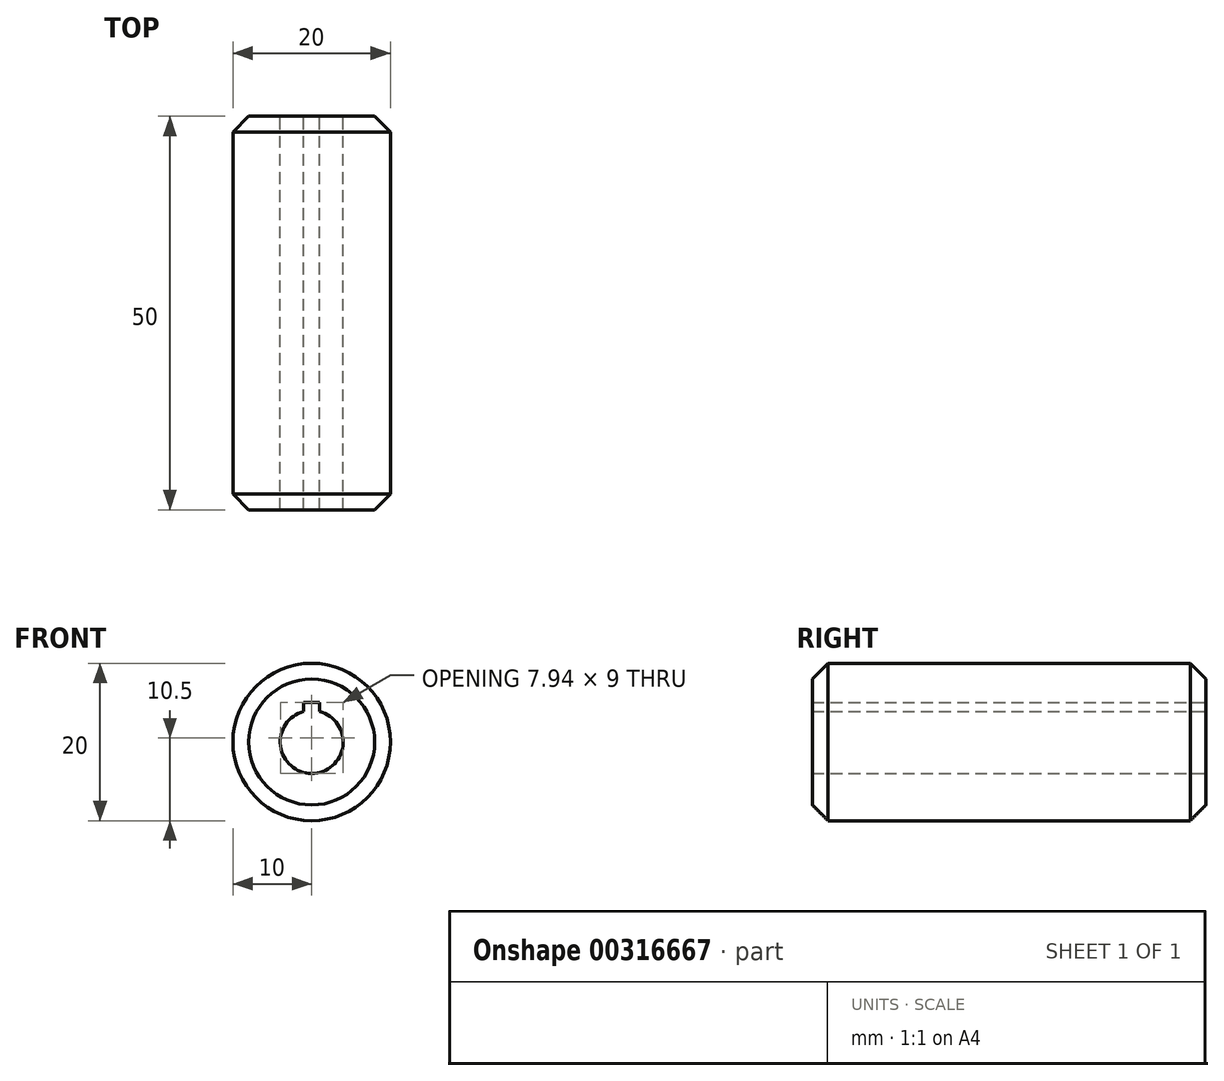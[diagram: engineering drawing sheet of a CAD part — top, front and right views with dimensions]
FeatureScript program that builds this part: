
annotation { "Feature Type Name" : "Feature", "Feature Type Description" : "" }
export const myFeature = defineFeature(function(context is Context, id is Id, definition is map)
    precondition{}
    {
        {
            var Q0;
            Q0=qCreatedBy(makeId("Front.planeOp"),FACE);
            var sketch = newSketch(context, id + "F0", { "sketchPlane" : qUnion([Q0])});
            skCircle(sketch, "E0", {"center": v(0, 0) * mm, "radius": 10 * mm});
            skSolve(sketch);
        }
        {
            var Q0;
            Q0 = qSketchRegion(id + "F0", true);
            extrude(context, id + "F1", {"entities" : qUnion([Q0]), "oppositeDirection" : true, "depth" : 50 * mm});
        }
        {
            var Q0;
            Q0=makeQuery(id+"F1.opExtrude","CAP_EDGE",EDGE,{"disambiguationData":[OSD([sQuery(id+"F0.wireOp",EDGE,"E0")])],"isStart":false});
            var Q1;
            Q1=makeQuery(id+"F1.opExtrude","CAP_EDGE",EDGE,{"disambiguationData":[OSD([sQuery(id+"F0.wireOp",EDGE,"E0")])],"isStart":true});
            chamfer(context, id + "F2", {"entities" : qUnion([Q0, Q1]), "width" : 2 * mm, "tangentPropagation" : true});
        }
        {
            var Q0;
            Q0=makeQuery(id+"F1.opExtrude","CAP_FACE",FACE,{"disambiguationData":[OSD([sQuery(id+"F0.wireOp",EDGE,"E0")])],"isStart":false});
            var sketch = newSketch(context, id + "F3", { "sketchPlane" : qUnion([Q0])});
            skArc(sketch, "E1", {"start": v(-1, 3.87) * mm, "mid": v(0, -4) * mm, "end": v(1, 3.87) * mm});
            skLineSegment(sketch, "E2.bottom", {"start": v(1, 5) * mm, "end": v(-1, 5) * mm});
            skLineSegment(sketch, "E2.left", {"start": v(1, 5) * mm, "end": v(1, 3.87) * mm});
            skLineSegment(sketch, "E2.right", {"start": v(-1, 5) * mm, "end": v(-1, 3.87) * mm});
            skPoint(sketch, "E2.middle", {"position": v(0, 4) * mm});
            skPoint(sketch, "E3.orphan", {"position": v(-1, 3) * mm});
            skPoint(sketch, "E4.orphan", {"position": v(1, 3) * mm});
            skSolve(sketch);
        }
        {
            var Q0;
            Q0 = qSketchRegion(id + "F3", true);
            extrude(context, id + "F4", {"entities" : qUnion([Q0]), "operationType" : NewBodyOperationType.REMOVE, "endBound" : BoundingType.UP_TO_NEXT, "oppositeDirection" : true, "depth" : 25 * mm});
        }
    });
